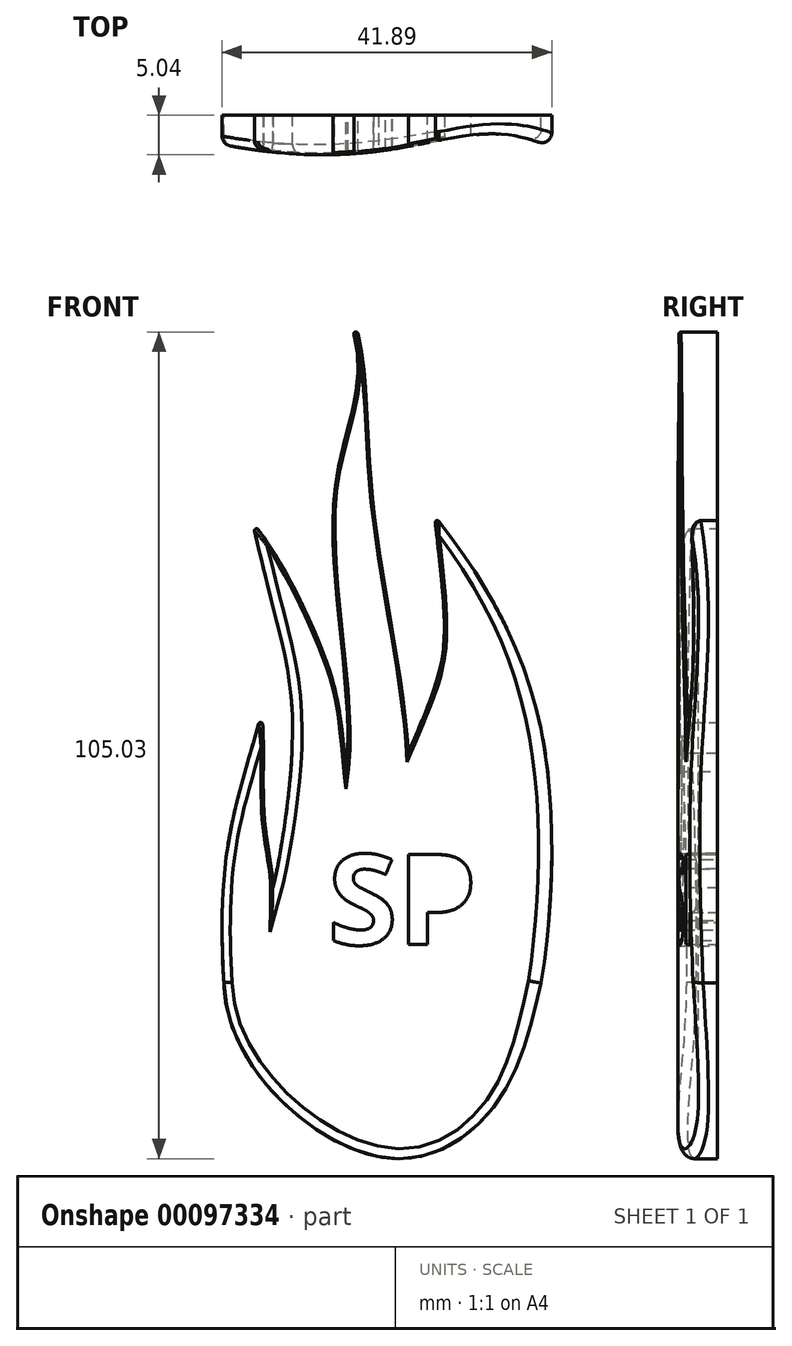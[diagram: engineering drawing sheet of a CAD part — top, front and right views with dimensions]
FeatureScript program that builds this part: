
annotation { "Feature Type Name" : "Feature", "Feature Type Description" : "" }
export const myFeature = defineFeature(function(context is Context, id is Id, definition is map)
    precondition{}
    {
        {
            var Q0;
            Q0=qCreatedBy(makeId("Front.planeOp"),FACE);
            var sketch = newSketch(context, id + "F0", { "sketchPlane" : qUnion([Q0])});
            skLineSegment(sketch, "E0", {"start": v(-18.77, 0) * mm, "end": v(21.52, 0) * mm});
            skFitSpline(sketch, "E1", {"points": [v(-18.77, 0) * mm, v(0, -21.92) * mm, v(13.64, -17.86) * mm, v(21.52, 0) * mm], "startDerivative": vector(1.03, -77.89) * mm, "endDerivative": vector(18.8, 84.6) * mm});
            skFitSpline(sketch, "E2", {"points": [v(-18.77, 0) * mm, v(-18.77, 13.2) * mm, v(-16.99, 23.55) * mm, v(-13.99, 34.23) * mm], "startDerivative": vector(-2.76, 41.93) * mm, "endDerivative": vector(5.02, 19.77) * mm});
            skFitSpline(sketch, "E3", {"points": [v(-13.99, 34.23) * mm, v(-13.64, 20.98) * mm, v(-12.57, 12.08) * mm], "startDerivative": vector(2.46, -17.69) * mm, "endDerivative": vector(-0.14, -15.6) * mm});
            skFitSpline(sketch, "E4", {"points": [v(-12.57, 12.08) * mm, v(-10.06, 31.48) * mm, v(-11.93, 45.32) * mm, v(-15.14, 58.43) * mm], "startDerivative": vector(6.66, 24.75) * mm, "endDerivative": vector(-14.12, 59.9) * mm});
            skFitSpline(sketch, "E5", {"points": [v(-15.14, 58.43) * mm, v(-5.57, 40.25) * mm, v(-3.28, 26.86) * mm], "startDerivative": vector(17.58, -19.89) * mm, "endDerivative": vector(3.97, -39.46) * mm});
            skFitSpline(sketch, "E6", {"points": [v(-3.28, 26.86) * mm, v(-4.7, 62.73) * mm, v(-3.28, 85.23) * mm], "startDerivative": vector(6.72, 51.87) * mm, "endDerivative": vector(-25.9, 58.88) * mm});
            skFitSpline(sketch, "E7", {"points": [v(-3.28, 85.23) * mm, v(0, 62.73) * mm, v(4.64, 29.17) * mm], "startDerivative": vector(18.6, -13.22) * mm, "endDerivative": vector(3.58, -60.77) * mm});
            skFitSpline(sketch, "E8", {"points": [v(4.64, 29.17) * mm, v(9.02, 41.8) * mm, v(7.97, 59.32) * mm], "startDerivative": vector(15, 36.03) * mm, "endDerivative": vector(-4.92, 43.3) * mm});
            skFitSpline(sketch, "E9", {"points": [v(19.48, -9.19) * mm, v(21.52, 0) * mm, v(21.98, 29.55) * mm, v(7.97, 59.32) * mm], "startDerivative": vector(9.04, 35.58) * mm, "endDerivative": vector(-56.82, 71.54) * mm});
            skText(sketch, "E10", { "text": "SP", "fontName": "OpenSans-Bold.ttf"});
            skLineSegment(sketch, "E11", {"start": v(-55.07, 81.2) * mm, "end": v(-55.07, -47.32) * mm, "construction": true});
            const initialGuessF0  = {"E10": [-0.00558, 0.00485, 1, 0, 0.01153]};
            skSetInitialGuess(sketch, initialGuessF0);
            skSolve(sketch);
        }
        {
            var Q0;
            Q0=qCreatedBy(makeId("Top.planeOp"),FACE);
            var sketch = newSketch(context, id + "F1", { "sketchPlane" : qUnion([Q0])});
            skFitSpline(sketch, "E12.0", {"points": [v(-18.77, -5.08) * mm, v(-18.64, -5.08) * mm, v(-0.83, -5.08) * mm, v(15.77, -5.08) * mm, v(19.48, -5.08) * mm, v(21.52, -5.08) * mm]});
            skLineSegment(sketch, "E13", {"start": v(21.52, -5.08) * mm, "end": v(24.61, -5.08) * mm});
            skFitSpline(sketch, "E14", {"points": [v(-20.61, -3.4) * mm, v(24.61, -5.08) * mm], "startDerivative": vector(80.39, -17.23) * mm, "endDerivative": vector(40.14, -23.02) * mm});
            skSolve(sketch);
        }
        {
            var Q0;
            Q0=sQuery(id+"F1.wireOp",EDGE,"E14");
            extrude(context, id + "F2", {"bodyType" : ToolBodyType.SURFACE, "surfaceEntities" : qUnion([Q0]), "depth" : 101.6 * mm, "hasSecondDirection" : true, "secondDirectionOppositeDirection" : true, "secondDirectionDepth" : 101.6 * mm});
        }
        {
            var Q0;
            {var subQ1=sQuery(id+"F0.wireOp",EDGE,"E0");Q0=makeQuery(id+"F0.imprint","IMPRINT",FACE,{"disambiguationData":[TD([[makeQuery(id+"F0.imprint","IMPRINT",EDGE,{"derivedFrom":subQ1}),1.0]])]});}
            var Q1;
            Q1=makeQuery(id+"F0.imprint","IMPRINT",FACE,{"disambiguationData":[TD([[makeQuery(id+"F0.imprint","IMPRINT",EDGE,{"derivedFrom":sQuery(id+"F0.wireOp",EDGE,"E0")}),-1.0]])]});
            extrude(context, id + "F3", {"entities" : qUnion([Q0, Q1]), "endBound" : BoundingType.UP_TO_NEXT, "depth" : 25.4 * mm});
        }
        {
            var Q0;
            Q0=makeQuery(id+"F3.opExtrude","CAP_EDGE",EDGE,{"disambiguationData":[OSD([sQuery(id+"F0.wireOp",EDGE,"E1")])],"isStart":false});
            var Q1;
            Q1=makeQuery(id+"F3.opExtrude","CAP_EDGE",EDGE,{"disambiguationData":[OSD([sQuery(id+"F0.wireOp",EDGE,"E9")])],"isStart":false});
            var Q2;
            Q2=makeQuery(id+"F3.opExtrude","CAP_EDGE",EDGE,{"disambiguationData":[OSD([sQuery(id+"F0.wireOp",EDGE,"E2")])],"isStart":false});
            fillet(context, id + "F4", {"entities" : qUnion([Q0, Q1, Q2]), "radius" : 1.27 * mm, "tangentPropagation" : true, "allowEdgeOverflow" : false});
        }
        {
            var Q0;
            Q0=makeQuery(id+"F3.opExtrude","CAP_EDGE",EDGE,{"disambiguationData":[OSD([sQuery(id+"F0.wireOp",EDGE,"E4")])],"isStart":false});
            fillet(context, id + "F5", {"entities" : qUnion([Q0]), "radius" : 1.27 * mm, "allowEdgeOverflow" : false});
        }
        {
            var Q0;
            Q0=makeQuery(id+"F3.opExtrude","CAP_EDGE",EDGE,{"disambiguationData":[OSD([sQuery(id+"F0.wireOp",EDGE,"E6")])],"isStart":false});
            fillet(context, id + "F6", {"entities" : qUnion([Q0]), "radius" : 0.25 * mm, "tangentPropagation" : true, "allowEdgeOverflow" : false});
        }
        {
            var Q0;
            Q0=makeQuery(id+"F3.opExtrude","CAP_EDGE",EDGE,{"disambiguationData":[OSD([sQuery(id+"F0.wireOp",EDGE,"E8")])],"isStart":false});
            var Q1;
            Q1=makeQuery(id+"F4.opFillet","BLEND_EDGE",EDGE,{"blendedFrom":[makeQuery(id+"F3.opExtrude","CAP_EDGE",EDGE,{"disambiguationData":[OSD([sQuery(id+"F0.wireOp",EDGE,"E9")])],"isStart":false}),makeQuery(id+"F3.opExtrude","SWEPT_FACE",FACE,{"disambiguationData":[OSD([sQuery(id+"F0.wireOp",EDGE,"E8")])]})],"blendedInto":[makeQuery(id+"F3.opExtrude","SWEPT_FACE",FACE,{"disambiguationData":[OSD([sQuery(id+"F0.wireOp",EDGE,"E8")])]})]});
            fillet(context, id + "F7", {"entities" : qUnion([Q0, Q1]), "radius" : 0.25 * mm, "tangentPropagation" : true, "allowEdgeOverflow" : false});
        }
        {
            var Q0;
            Q0=makeQuery(id+"F3.opExtrude","CAP_EDGE",EDGE,{"disambiguationData":[OSD([sQuery(id+"F0.wireOp",EDGE,"E3")])],"isStart":false});
            var Q1;
            Q1=makeQuery(id+"F4.opFillet","BLEND_EDGE",EDGE,{"blendedFrom":[makeQuery(id+"F3.opExtrude","CAP_EDGE",EDGE,{"disambiguationData":[OSD([sQuery(id+"F0.wireOp",EDGE,"E2")])],"isStart":false}),makeQuery(id+"F3.opExtrude","SWEPT_FACE",FACE,{"disambiguationData":[OSD([sQuery(id+"F0.wireOp",EDGE,"E3")])]})],"blendedInto":[makeQuery(id+"F3.opExtrude","SWEPT_FACE",FACE,{"disambiguationData":[OSD([sQuery(id+"F0.wireOp",EDGE,"E3")])]})]});
            fillet(context, id + "F8", {"entities" : qUnion([Q0, Q1]), "radius" : 0.25 * mm, "tangentPropagation" : true, "allowEdgeOverflow" : false});
        }
        {
            var Q0;
            Q0=makeQuery(id+"F3.opExtrude","CAP_EDGE",EDGE,{"disambiguationData":[OSD([sQuery(id+"F0.wireOp",EDGE,"E5")])],"isStart":false});
            var Q1;
            Q1=makeQuery(id+"F5.opFillet","BLEND_EDGE",EDGE,{"blendedFrom":[makeQuery(id+"F3.opExtrude","CAP_EDGE",EDGE,{"disambiguationData":[OSD([sQuery(id+"F0.wireOp",EDGE,"E4")])],"isStart":false}),makeQuery(id+"F3.opExtrude","SWEPT_FACE",FACE,{"disambiguationData":[OSD([sQuery(id+"F0.wireOp",EDGE,"E5")])]})],"blendedInto":[makeQuery(id+"F3.opExtrude","SWEPT_FACE",FACE,{"disambiguationData":[OSD([sQuery(id+"F0.wireOp",EDGE,"E5")])]})]});
            fillet(context, id + "F9", {"entities" : qUnion([Q0, Q1]), "radius" : 0.25 * mm, "tangentPropagation" : true, "allowEdgeOverflow" : false});
        }
        {
            var Q0;
            Q0=makeQuery(id+"F3.opExtrude","SWEPT_EDGE",EDGE,{"disambiguationData":[OSD([sQuery(id+"F0.wireOp",EDGE,"E6"),sQuery(id+"F0.wireOp",EDGE,"E7")])]});
            fillet(context, id + "F10", {"entities" : qUnion([Q0]), "radius" : 0.25 * mm, "tangentPropagation" : true, "allowEdgeOverflow" : false});
        }
    });
